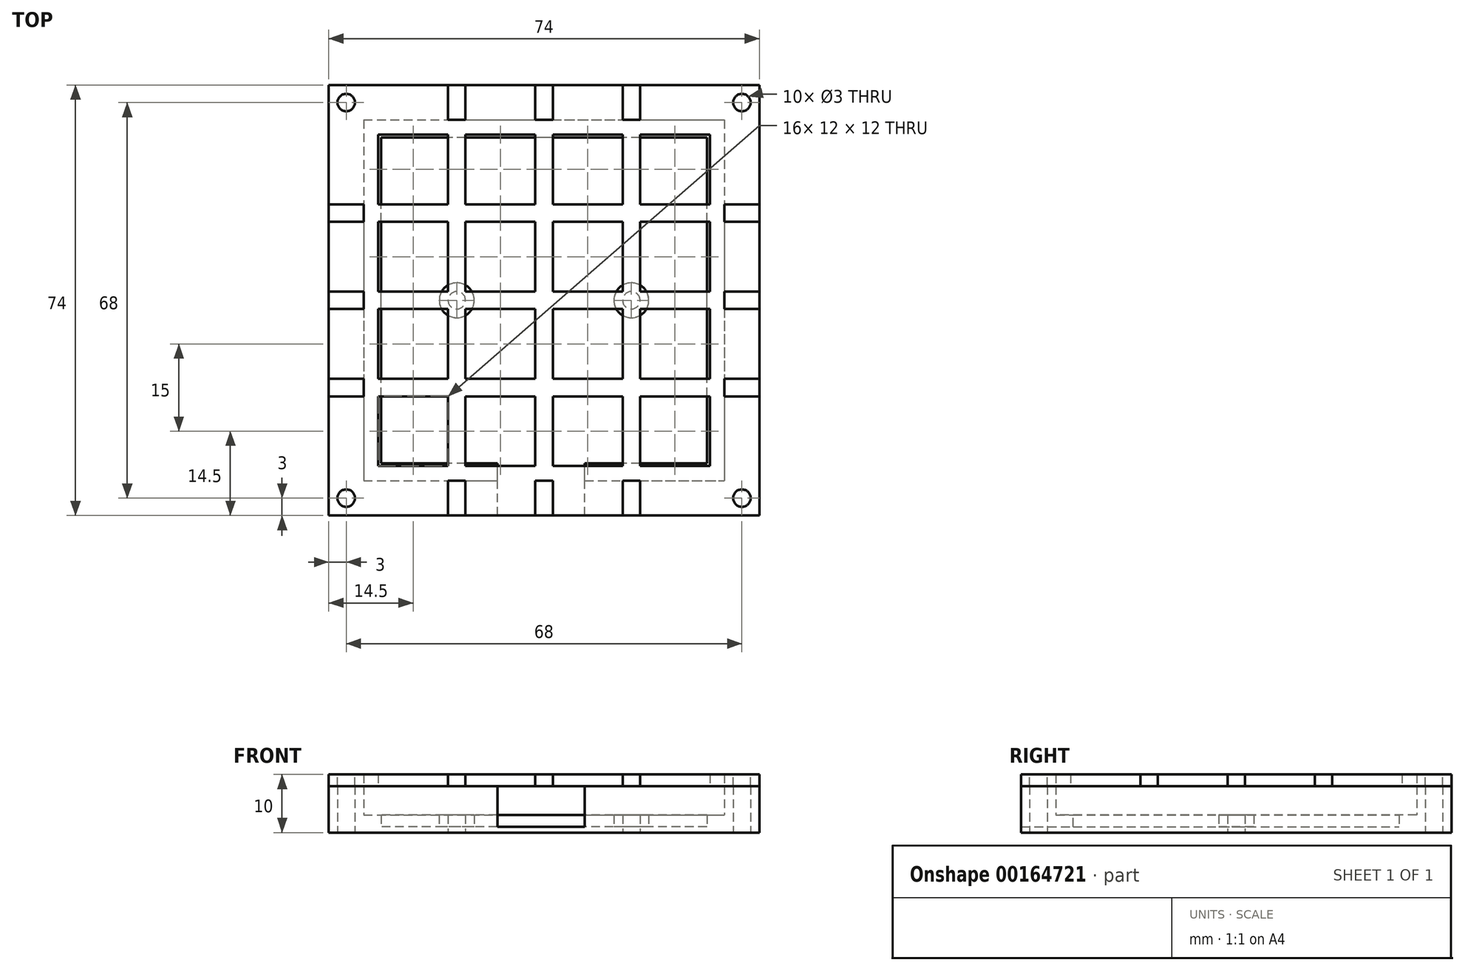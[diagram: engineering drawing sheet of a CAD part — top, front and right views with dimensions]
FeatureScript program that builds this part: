
annotation { "Feature Type Name" : "Feature", "Feature Type Description" : "" }
export const myFeature = defineFeature(function(context is Context, id is Id, definition is map)
    precondition{}
    {
        {
            var Q0;
            Q0=qCreatedBy(makeId("Top.planeOp"),FACE);
            var sketch = newSketch(context, id + "F0", { "sketchPlane" : qUnion([Q0])});
            skLineSegment(sketch, "E0.bottom", {"start": v(-31, 31) * mm, "end": v(31, 31) * mm});
            skLineSegment(sketch, "E0.top", {"start": v(-31, -31) * mm, "end": v(31, -31) * mm});
            skLineSegment(sketch, "E0.left", {"start": v(-31, 31) * mm, "end": v(-31, -31) * mm});
            skLineSegment(sketch, "E0.right", {"start": v(31, 31) * mm, "end": v(31, -31) * mm});
            skPoint(sketch, "E0.middle", {"position": v(0, 0) * mm});
            skLineSegment(sketch, "E1.bottom", {"start": v(-37, 37) * mm, "end": v(37, 37) * mm});
            skLineSegment(sketch, "E1.top", {"start": v(-37, -37) * mm, "end": v(37, -37) * mm});
            skLineSegment(sketch, "E1.left", {"start": v(-37, 37) * mm, "end": v(-37, -37) * mm});
            skLineSegment(sketch, "E1.right", {"start": v(37, 37) * mm, "end": v(37, -37) * mm});
            skCircle(sketch, "E2", {"center": v(34, 34) * mm, "radius": 1.5 * mm});
            skCircle(sketch, "E3", {"center": v(34, -34) * mm, "radius": 1.5 * mm});
            skCircle(sketch, "E4", {"center": v(-34, -34) * mm, "radius": 1.5 * mm});
            skCircle(sketch, "E5", {"center": v(-34, 34) * mm, "radius": 1.5 * mm});
            skCircle(sketch, "E6", {"center": v(-15, 0) * mm, "radius": 1.5 * mm});
            skCircle(sketch, "E7", {"center": v(15, 0) * mm, "radius": 1.5 * mm});
            skLineSegment(sketch, "E8", {"start": v(15, 0) * mm, "end": v(-15, 0) * mm, "construction": true});
            skCircle(sketch, "E9", {"center": v(-15, 0) * mm, "radius": 3 * mm});
            skCircle(sketch, "E10", {"center": v(15, 0) * mm, "radius": 3 * mm});
            skLineSegment(sketch, "E11.bottom", {"start": v(28, -28) * mm, "end": v(-28, -28) * mm});
            skLineSegment(sketch, "E11.top", {"start": v(28, 28) * mm, "end": v(-28, 28) * mm});
            skLineSegment(sketch, "E11.left", {"start": v(28, -28) * mm, "end": v(28, 28) * mm});
            skLineSegment(sketch, "E11.right", {"start": v(-28, -28) * mm, "end": v(-28, 28) * mm});
            skLineSegment(sketch, "E12", {"start": v(31, 31) * mm, "end": v(34, 31) * mm, "construction": true});
            skLineSegment(sketch, "E13", {"start": v(34, 31) * mm, "end": v(34, 34) * mm, "construction": true});
            skLineSegment(sketch, "E14", {"start": v(-31, 31) * mm, "end": v(-34, 31) * mm, "construction": true});
            skLineSegment(sketch, "E15", {"start": v(-34, 31) * mm, "end": v(-34, 34) * mm, "construction": true});
            skLineSegment(sketch, "E16", {"start": v(-31, -31) * mm, "end": v(-34, -31) * mm, "construction": true});
            skLineSegment(sketch, "E17", {"start": v(-34, -31) * mm, "end": v(-34, -34) * mm, "construction": true});
            skLineSegment(sketch, "E18", {"start": v(31, -31) * mm, "end": v(34, -31) * mm, "construction": true});
            skLineSegment(sketch, "E19", {"start": v(34, -31) * mm, "end": v(34, -34) * mm, "construction": true});
            skSolve(sketch);
        }
        {
            var Q0;
            Q0=makeQuery(id+"F0.imprint","IMPRINT",FACE,{"disambiguationData":[TD([[makeQuery(id+"F0.imprint","IMPRINT",EDGE,{"derivedFrom":sQuery(id+"F0.wireOp",EDGE,"E0.bottom")}),1.0]])]});
            extrude(context, id + "F1", {"entities" : qUnion([Q0]), "depth" : 8 * mm});
        }
        {
            var Q0;
            Q0=makeQuery(id+"F0.imprint","IMPRINT",FACE,{"disambiguationData":[TD([[makeQuery(id+"F0.imprint","IMPRINT",EDGE,{"derivedFrom":sQuery(id+"F0.wireOp",EDGE,"E0.bottom")}),-1.0]])]});
            extrude(context, id + "F2", {"entities" : qUnion([Q0]), "operationType" : NewBodyOperationType.ADD, "depth" : 2 * mm});
        }
        {
            var Q0;
            Q0=makeQuery(id+"F0.imprint","IMPRINT",FACE,{"disambiguationData":[TD([[makeQuery(id+"F0.imprint","IMPRINT",EDGE,{"derivedFrom":sQuery(id+"F0.wireOp",EDGE,"E9")}),-1.0]])]});
            extrude(context, id + "F3", {"entities" : qUnion([Q0]), "operationType" : NewBodyOperationType.ADD, "depth" : 1 * mm});
        }
        {
            var Q0;
            Q0=makeQuery(id+"F0.imprint","IMPRINT",FACE,{"disambiguationData":[TD([[makeQuery(id+"F0.imprint","IMPRINT",EDGE,{"derivedFrom":sQuery(id+"F0.wireOp",EDGE,"E6")}),-1.0]])]});
            var Q1;
            Q1=makeQuery(id+"F0.imprint","IMPRINT",FACE,{"disambiguationData":[TD([[makeQuery(id+"F0.imprint","IMPRINT",EDGE,{"derivedFrom":sQuery(id+"F0.wireOp",EDGE,"E7")}),-1.0]])]});
            extrude(context, id + "F4", {"entities" : qUnion([Q0, Q1]), "operationType" : NewBodyOperationType.ADD, "depth" : 3 * mm});
        }
        {
            var Q0;
            Q0=makeQuery(id+"F0.imprint","IMPRINT",FACE,{"disambiguationData":[TD([[makeQuery(id+"F0.imprint","IMPRINT",EDGE,{"derivedFrom":sQuery(id+"F0.wireOp",EDGE,"E0.bottom")}),-1.0]])]});
            extrude(context, id + "F5", {"entities" : qUnion([Q0]), "operationType" : NewBodyOperationType.ADD, "depth" : 3 * mm});
        }
        {
            var Q0;
            Q0=makeQuery(id+"F1.opExtrude","CAP_FACE",FACE,{"disambiguationData":[OSD([sQuery(id+"F0.wireOp",EDGE,"E0.bottom"),sQuery(id+"F0.wireOp",EDGE,"E0.top"),sQuery(id+"F0.wireOp",EDGE,"E0.left"),sQuery(id+"F0.wireOp",EDGE,"E0.right"),sQuery(id+"F0.wireOp",EDGE,"E1.bottom"),sQuery(id+"F0.wireOp",EDGE,"E1.top"),sQuery(id+"F0.wireOp",EDGE,"E1.left"),sQuery(id+"F0.wireOp",EDGE,"E1.right"),sQuery(id+"F0.wireOp",EDGE,"E2"),sQuery(id+"F0.wireOp",EDGE,"E3"),sQuery(id+"F0.wireOp",EDGE,"E4"),sQuery(id+"F0.wireOp",EDGE,"E5")])],"isStart":false});
            var sketch = newSketch(context, id + "F6", { "sketchPlane" : qUnion([Q0])});
            skLineSegment(sketch, "E20", {"start": v(-0.5, -37) * mm, "end": v(-0.5, -31) * mm, "construction": true});
            skLineSegment(sketch, "E21.0", {"start": v(28, -28) * mm, "end": v(-28, -28) * mm});
            skLineSegment(sketch, "E22.bottom", {"start": v(-0.5, -37) * mm, "end": v(-8, -37) * mm});
            skLineSegment(sketch, "E22.top", {"start": v(-0.5, -28) * mm, "end": v(-8, -28) * mm});
            skLineSegment(sketch, "E22.left", {"start": v(-0.5, -37) * mm, "end": v(-0.5, -28) * mm});
            skLineSegment(sketch, "E22.right", {"start": v(-8, -37) * mm, "end": v(-8, -28) * mm});
            skLineSegment(sketch, "E23.bottom", {"start": v(-0.5, -37) * mm, "end": v(7, -37) * mm});
            skLineSegment(sketch, "E23.top", {"start": v(-0.5, -28) * mm, "end": v(7, -28) * mm});
            skLineSegment(sketch, "E23.right", {"start": v(7, -37) * mm, "end": v(7, -28) * mm});
            skSolve(sketch);
        }
        {
            var Q0;
            Q0=makeQuery(id+"F1.opExtrude","CAP_FACE",FACE,{"disambiguationData":[OSD([sQuery(id+"F0.wireOp",EDGE,"E0.bottom"),sQuery(id+"F0.wireOp",EDGE,"E0.top"),sQuery(id+"F0.wireOp",EDGE,"E0.left"),sQuery(id+"F0.wireOp",EDGE,"E0.right"),sQuery(id+"F0.wireOp",EDGE,"E1.bottom"),sQuery(id+"F0.wireOp",EDGE,"E1.top"),sQuery(id+"F0.wireOp",EDGE,"E1.left"),sQuery(id+"F0.wireOp",EDGE,"E1.right"),sQuery(id+"F0.wireOp",EDGE,"E2"),sQuery(id+"F0.wireOp",EDGE,"E3"),sQuery(id+"F0.wireOp",EDGE,"E4"),sQuery(id+"F0.wireOp",EDGE,"E5")])],"isStart":false});
            var sketch = newSketch(context, id + "F7", { "sketchPlane" : qUnion([Q0])});
            skLineSegment(sketch, "E24.bottom", {"start": v(-37, 37) * mm, "end": v(37, 37) * mm});
            skLineSegment(sketch, "E24.top", {"start": v(-37, -37) * mm, "end": v(37, -37) * mm});
            skLineSegment(sketch, "E24.left", {"start": v(-37, 37) * mm, "end": v(-37, -37) * mm});
            skLineSegment(sketch, "E24.right", {"start": v(37, 37) * mm, "end": v(37, -37) * mm});
            skLineSegment(sketch, "E25", {"start": v(-15, 37) * mm, "end": v(-15, -36.5) * mm, "construction": true});
            skLineSegment(sketch, "E26", {"start": v(0, 37) * mm, "end": v(0, -37) * mm, "construction": true});
            skLineSegment(sketch, "E27", {"start": v(15, 37) * mm, "end": v(15, -37) * mm, "construction": true});
            skLineSegment(sketch, "E28", {"start": v(-31, 0) * mm, "end": v(31, 0) * mm, "construction": true});
            skLineSegment(sketch, "E29", {"start": v(-31, 15) * mm, "end": v(31, 15) * mm, "construction": true});
            skLineSegment(sketch, "E30", {"start": v(-31, -15) * mm, "end": v(31, -15) * mm, "construction": true});
            skLineSegment(sketch, "E31.bottom", {"start": v(-16.5, 37) * mm, "end": v(-13.5, 37) * mm});
            skLineSegment(sketch, "E31.top", {"start": v(-16.5, -37) * mm, "end": v(-13.5, -37) * mm});
            skLineSegment(sketch, "E31.left", {"start": v(-16.5, 37) * mm, "end": v(-16.5, -37) * mm});
            skLineSegment(sketch, "E31.right", {"start": v(-13.5, 37) * mm, "end": v(-13.5, -37) * mm});
            skLineSegment(sketch, "E32.bottom", {"start": v(-1.5, 37) * mm, "end": v(1.5, 37) * mm});
            skLineSegment(sketch, "E32.top", {"start": v(-1.5, -37) * mm, "end": v(1.5, -37) * mm});
            skLineSegment(sketch, "E32.left", {"start": v(-1.5, 37) * mm, "end": v(-1.5, -37) * mm});
            skLineSegment(sketch, "E32.right", {"start": v(1.5, 37) * mm, "end": v(1.5, -37) * mm});
            skLineSegment(sketch, "E33.bottom", {"start": v(13.5, 37) * mm, "end": v(16.5, 37) * mm});
            skLineSegment(sketch, "E33.top", {"start": v(13.5, -37) * mm, "end": v(16.5, -37) * mm});
            skLineSegment(sketch, "E33.left", {"start": v(13.5, 37) * mm, "end": v(13.5, -37) * mm});
            skLineSegment(sketch, "E33.right", {"start": v(16.5, 37) * mm, "end": v(16.5, -37) * mm});
            skLineSegment(sketch, "E34.bottom", {"start": v(-37, 13.5) * mm, "end": v(37, 13.5) * mm});
            skLineSegment(sketch, "E34.top", {"start": v(-37, 16.5) * mm, "end": v(37, 16.5) * mm});
            skLineSegment(sketch, "E34.left", {"start": v(-37, 13.5) * mm, "end": v(-37, 16.5) * mm});
            skLineSegment(sketch, "E34.right", {"start": v(37, 13.5) * mm, "end": v(37, 16.5) * mm});
            skLineSegment(sketch, "E35.bottom", {"start": v(-37, -1.5) * mm, "end": v(37, -1.5) * mm});
            skLineSegment(sketch, "E35.top", {"start": v(-37, 1.5) * mm, "end": v(37, 1.5) * mm});
            skLineSegment(sketch, "E35.left", {"start": v(-37, -1.5) * mm, "end": v(-37, 1.5) * mm});
            skLineSegment(sketch, "E35.right", {"start": v(37, -1.5) * mm, "end": v(37, 1.5) * mm});
            skLineSegment(sketch, "E36.bottom", {"start": v(-37, -16.5) * mm, "end": v(37, -16.5) * mm});
            skLineSegment(sketch, "E36.top", {"start": v(-37, -13.5) * mm, "end": v(37, -13.5) * mm});
            skLineSegment(sketch, "E36.left", {"start": v(-37, -16.5) * mm, "end": v(-37, -13.5) * mm});
            skLineSegment(sketch, "E36.right", {"start": v(37, -16.5) * mm, "end": v(37, -13.5) * mm});
            skLineSegment(sketch, "E37", {"start": v(-31, -15) * mm, "end": v(-37, -15) * mm, "construction": true});
            skLineSegment(sketch, "E38", {"start": v(-31, 0) * mm, "end": v(-37, 0) * mm, "construction": true});
            skLineSegment(sketch, "E39", {"start": v(-31, 15) * mm, "end": v(-37, 15) * mm, "construction": true});
            skLineSegment(sketch, "E40.bottom", {"start": v(28.5, -28.5) * mm, "end": v(-28.5, -28.5) * mm});
            skLineSegment(sketch, "E40.top", {"start": v(28.5, 28.5) * mm, "end": v(-28.5, 28.5) * mm});
            skLineSegment(sketch, "E40.left", {"start": v(28.5, -28.5) * mm, "end": v(28.5, 28.5) * mm});
            skLineSegment(sketch, "E40.right", {"start": v(-28.5, -28.5) * mm, "end": v(-28.5, 28.5) * mm});
            skPoint(sketch, "E40.middle", {"position": v(0, 0) * mm});
            skSolve(sketch);
        }
        {
            var Q0;
            Q0=makeQuery(id+"F7.imprint","IMPRINT",FACE,{"disambiguationData":[TD([[makeQuery(id+"F7.imprint","IMPRINT",EDGE,{"derivedFrom":makeQuery(id+"F1.opExtrude","CAP_EDGE",EDGE,{"disambiguationData":[OSD([sQuery(id+"F0.wireOp",EDGE,"E5")])],"isStart":false})}),-1.0]])]});
            var Q1;
            {var subQ0=sQuery(id+"F7.wireOp",EDGE,"E31.right");var subQ5=makeQuery(id+"F1.opExtrude","CAP_EDGE",EDGE,{"disambiguationData":[OSD([sQuery(id+"F0.wireOp",EDGE,"E0.bottom")])],"isStart":false});var subQ6=makeQuery(id+"F7.imprint","INTERSECT",VERTEX,{"derivedFrom":[subQ5,subQ0]});Q1=makeQuery(id+"F7.imprint","IMPRINT",FACE,{"disambiguationData":[TD([[makeQuery(id+"F7.imprint","IMPRINT",EDGE,{"disambiguationData":[TD([[subQ6,-1.0]])],"derivedFrom":subQ5}),1.0]])]});}
            var Q2;
            {var subQ0=sQuery(id+"F7.wireOp",EDGE,"E31.bottom");Q2=makeQuery(id+"F7.imprint","IMPRINT",FACE,{"disambiguationData":[TD([[makeQuery(id+"F7.imprint","IMPRINT",EDGE,{"derivedFrom":subQ0}),-1.0]])]});}
            var Q3;
            {var subQ0=sQuery(id+"F7.wireOp",EDGE,"E32.bottom");Q3=makeQuery(id+"F7.imprint","IMPRINT",FACE,{"disambiguationData":[TD([[makeQuery(id+"F7.imprint","IMPRINT",EDGE,{"derivedFrom":subQ0}),-1.0]])]});}
            var Q4;
            {var subQ0=sQuery(id+"F7.wireOp",EDGE,"E32.right");var subQ5=makeQuery(id+"F1.opExtrude","CAP_EDGE",EDGE,{"disambiguationData":[OSD([sQuery(id+"F0.wireOp",EDGE,"E0.bottom")])],"isStart":false});var subQ6=makeQuery(id+"F7.imprint","INTERSECT",VERTEX,{"derivedFrom":[subQ5,subQ0]});Q4=makeQuery(id+"F7.imprint","IMPRINT",FACE,{"disambiguationData":[TD([[makeQuery(id+"F7.imprint","IMPRINT",EDGE,{"disambiguationData":[TD([[subQ6,-1.0]])],"derivedFrom":subQ5}),1.0]])]});}
            var Q5;
            {var subQ0=sQuery(id+"F7.wireOp",EDGE,"E33.bottom");Q5=makeQuery(id+"F7.imprint","IMPRINT",FACE,{"disambiguationData":[TD([[makeQuery(id+"F7.imprint","IMPRINT",EDGE,{"derivedFrom":subQ0}),-1.0]])]});}
            var Q6;
            Q6=makeQuery(id+"F7.imprint","IMPRINT",FACE,{"disambiguationData":[TD([[makeQuery(id+"F7.imprint","IMPRINT",EDGE,{"derivedFrom":makeQuery(id+"F1.opExtrude","CAP_EDGE",EDGE,{"disambiguationData":[OSD([sQuery(id+"F0.wireOp",EDGE,"E2")])],"isStart":false})}),-1.0]])]});
            var Q7;
            {var subQ1=sQuery(id+"F7.wireOp",EDGE,"E40.top");var subQ5=sQuery(id+"F7.wireOp",EDGE,"E33.right");var subQ6=makeQuery(id+"F7.imprint","INTERSECT",VERTEX,{"derivedFrom":[subQ5,subQ1]});Q7=makeQuery(id+"F7.imprint","IMPRINT",FACE,{"disambiguationData":[TD([[makeQuery(id+"F7.imprint","IMPRINT",EDGE,{"disambiguationData":[TD([[subQ6,1.0]])],"derivedFrom":subQ5}),1.0]])]});}
            var Q8;
            {var subQ0=sQuery(id+"F7.wireOp",EDGE,"E40.top");var subQ1=sQuery(id+"F7.wireOp",EDGE,"E33.left");var subQ2=makeQuery(id+"F7.imprint","INTERSECT",VERTEX,{"derivedFrom":[subQ1,subQ0]});Q8=makeQuery(id+"F7.imprint","IMPRINT",FACE,{"disambiguationData":[TD([[makeQuery(id+"F7.imprint","IMPRINT",EDGE,{"disambiguationData":[TD([[subQ2,1.0]])],"derivedFrom":subQ1}),1.0]])]});}
            var Q9;
            {var subQ0=sQuery(id+"F7.wireOp",EDGE,"E40.top");var subQ1=sQuery(id+"F7.wireOp",EDGE,"E32.right");var subQ2=makeQuery(id+"F7.imprint","INTERSECT",VERTEX,{"derivedFrom":[subQ1,subQ0]});Q9=makeQuery(id+"F7.imprint","IMPRINT",FACE,{"disambiguationData":[TD([[makeQuery(id+"F7.imprint","IMPRINT",EDGE,{"disambiguationData":[TD([[subQ2,1.0]])],"derivedFrom":subQ1}),1.0]])]});}
            var Q10;
            {var subQ0=sQuery(id+"F7.wireOp",EDGE,"E40.top");var subQ1=sQuery(id+"F7.wireOp",EDGE,"E32.left");var subQ2=makeQuery(id+"F7.imprint","INTERSECT",VERTEX,{"derivedFrom":[subQ1,subQ0]});Q10=makeQuery(id+"F7.imprint","IMPRINT",FACE,{"disambiguationData":[TD([[makeQuery(id+"F7.imprint","IMPRINT",EDGE,{"disambiguationData":[TD([[subQ2,1.0]])],"derivedFrom":subQ1}),1.0]])]});}
            var Q11;
            {var subQ0=sQuery(id+"F7.wireOp",EDGE,"E40.top");var subQ1=sQuery(id+"F7.wireOp",EDGE,"E31.right");var subQ2=makeQuery(id+"F7.imprint","INTERSECT",VERTEX,{"derivedFrom":[subQ1,subQ0]});Q11=makeQuery(id+"F7.imprint","IMPRINT",FACE,{"disambiguationData":[TD([[makeQuery(id+"F7.imprint","IMPRINT",EDGE,{"disambiguationData":[TD([[subQ2,1.0]])],"derivedFrom":subQ1}),1.0]])]});}
            var Q12;
            {var subQ0=sQuery(id+"F7.wireOp",EDGE,"E40.top");var subQ1=sQuery(id+"F7.wireOp",EDGE,"E31.left");var subQ2=makeQuery(id+"F7.imprint","INTERSECT",VERTEX,{"derivedFrom":[subQ1,subQ0]});Q12=makeQuery(id+"F7.imprint","IMPRINT",FACE,{"disambiguationData":[TD([[makeQuery(id+"F7.imprint","IMPRINT",EDGE,{"disambiguationData":[TD([[subQ2,1.0]])],"derivedFrom":subQ1}),1.0]])]});}
            var Q13;
            {var subQ5=sQuery(id+"F7.wireOp",EDGE,"E40.top");var subQ7=sQuery(id+"F7.wireOp",EDGE,"E31.left");var subQ8=makeQuery(id+"F7.imprint","INTERSECT",VERTEX,{"derivedFrom":[subQ7,subQ5]});Q13=makeQuery(id+"F7.imprint","IMPRINT",FACE,{"disambiguationData":[TD([[makeQuery(id+"F7.imprint","IMPRINT",EDGE,{"disambiguationData":[TD([[subQ8,1.0]])],"derivedFrom":subQ7}),-1.0]])]});}
            var Q14;
            {var subQ0=sQuery(id+"F7.wireOp",EDGE,"E34.left");Q14=makeQuery(id+"F7.imprint","IMPRINT",FACE,{"disambiguationData":[TD([[makeQuery(id+"F7.imprint","IMPRINT",EDGE,{"derivedFrom":subQ0}),1.0]])]});}
            var Q15;
            {var subQ0=sQuery(id+"F7.wireOp",EDGE,"E40.right");var subQ1=sQuery(id+"F7.wireOp",EDGE,"E34.bottom");var subQ2=makeQuery(id+"F7.imprint","INTERSECT",VERTEX,{"derivedFrom":[subQ1,subQ0]});Q15=makeQuery(id+"F7.imprint","IMPRINT",FACE,{"disambiguationData":[TD([[makeQuery(id+"F7.imprint","IMPRINT",EDGE,{"disambiguationData":[TD([[subQ2,1.0]])],"derivedFrom":subQ1}),1.0]])]});}
            var Q16;
            {var subQ0=sQuery(id+"F7.wireOp",EDGE,"E35.left");Q16=makeQuery(id+"F7.imprint","IMPRINT",FACE,{"disambiguationData":[TD([[makeQuery(id+"F7.imprint","IMPRINT",EDGE,{"derivedFrom":subQ0}),1.0]])]});}
            var Q17;
            {var subQ0=sQuery(id+"F7.wireOp",EDGE,"E40.right");var subQ1=sQuery(id+"F7.wireOp",EDGE,"E35.bottom");var subQ2=makeQuery(id+"F7.imprint","INTERSECT",VERTEX,{"derivedFrom":[subQ1,subQ0]});Q17=makeQuery(id+"F7.imprint","IMPRINT",FACE,{"disambiguationData":[TD([[makeQuery(id+"F7.imprint","IMPRINT",EDGE,{"disambiguationData":[TD([[subQ2,1.0]])],"derivedFrom":subQ1}),1.0]])]});}
            var Q18;
            {var subQ0=sQuery(id+"F7.wireOp",EDGE,"E34.bottom");var subQ5=makeQuery(id+"F1.opExtrude","CAP_EDGE",EDGE,{"disambiguationData":[OSD([sQuery(id+"F0.wireOp",EDGE,"E0.left")])],"isStart":false});var subQ7=makeQuery(id+"F7.imprint","INTERSECT",VERTEX,{"derivedFrom":[subQ5,subQ0]});Q18=makeQuery(id+"F7.imprint","IMPRINT",FACE,{"disambiguationData":[TD([[makeQuery(id+"F7.imprint","IMPRINT",EDGE,{"disambiguationData":[TD([[subQ7,-1.0]])],"derivedFrom":subQ5}),-1.0]])]});}
            var Q19;
            {var subQ0=sQuery(id+"F7.wireOp",EDGE,"E40.right");var subQ1=sQuery(id+"F7.wireOp",EDGE,"E34.bottom");var subQ2=makeQuery(id+"F7.imprint","INTERSECT",VERTEX,{"derivedFrom":[subQ1,subQ0]});Q19=makeQuery(id+"F7.imprint","IMPRINT",FACE,{"disambiguationData":[TD([[makeQuery(id+"F7.imprint","IMPRINT",EDGE,{"disambiguationData":[TD([[subQ2,1.0]])],"derivedFrom":subQ1}),-1.0]])]});}
            var Q20;
            {var subQ0=sQuery(id+"F7.wireOp",EDGE,"E35.bottom");var subQ5=makeQuery(id+"F1.opExtrude","CAP_EDGE",EDGE,{"disambiguationData":[OSD([sQuery(id+"F0.wireOp",EDGE,"E0.left")])],"isStart":false});var subQ6=makeQuery(id+"F7.imprint","INTERSECT",VERTEX,{"derivedFrom":[subQ5,subQ0]});Q20=makeQuery(id+"F7.imprint","IMPRINT",FACE,{"disambiguationData":[TD([[makeQuery(id+"F7.imprint","IMPRINT",EDGE,{"disambiguationData":[TD([[subQ6,-1.0]])],"derivedFrom":subQ5}),-1.0]])]});}
            var Q21;
            {var subQ0=sQuery(id+"F7.wireOp",EDGE,"E40.right");var subQ1=sQuery(id+"F7.wireOp",EDGE,"E35.bottom");var subQ2=makeQuery(id+"F7.imprint","INTERSECT",VERTEX,{"derivedFrom":[subQ1,subQ0]});Q21=makeQuery(id+"F7.imprint","IMPRINT",FACE,{"disambiguationData":[TD([[makeQuery(id+"F7.imprint","IMPRINT",EDGE,{"disambiguationData":[TD([[subQ2,1.0]])],"derivedFrom":subQ1}),-1.0]])]});}
            var Q22;
            {var subQ0=sQuery(id+"F7.wireOp",EDGE,"E36.left");Q22=makeQuery(id+"F7.imprint","IMPRINT",FACE,{"disambiguationData":[TD([[makeQuery(id+"F7.imprint","IMPRINT",EDGE,{"derivedFrom":subQ0}),1.0]])]});}
            var Q23;
            {var subQ0=sQuery(id+"F7.wireOp",EDGE,"E40.right");var subQ1=sQuery(id+"F7.wireOp",EDGE,"E36.bottom");var subQ2=makeQuery(id+"F7.imprint","INTERSECT",VERTEX,{"derivedFrom":[subQ1,subQ0]});Q23=makeQuery(id+"F7.imprint","IMPRINT",FACE,{"disambiguationData":[TD([[makeQuery(id+"F7.imprint","IMPRINT",EDGE,{"disambiguationData":[TD([[subQ2,1.0]])],"derivedFrom":subQ1}),1.0]])]});}
            var Q24;
            {var subQ3=sQuery(id+"F0.wireOp",EDGE,"E4");Q24=makeQuery(id+"F7.imprint","IMPRINT",FACE,{"disambiguationData":[TD([[makeQuery(id+"F7.imprint","IMPRINT",EDGE,{"derivedFrom":makeQuery(id+"F1.opExtrude","CAP_EDGE",EDGE,{"disambiguationData":[OSD([subQ3])],"isStart":false})}),-1.0]])]});}
            var Q25;
            {var subQ0=sQuery(id+"F7.wireOp",EDGE,"E40.right");var subQ3=sQuery(id+"F7.wireOp",EDGE,"E36.bottom");var subQ4=makeQuery(id+"F7.imprint","INTERSECT",VERTEX,{"derivedFrom":[subQ3,subQ0]});Q25=makeQuery(id+"F7.imprint","IMPRINT",FACE,{"disambiguationData":[TD([[makeQuery(id+"F7.imprint","IMPRINT",EDGE,{"disambiguationData":[TD([[subQ4,1.0]])],"derivedFrom":subQ3}),-1.0]])]});}
            var Q26;
            {var subQ0=sQuery(id+"F7.wireOp",EDGE,"E31.top");Q26=makeQuery(id+"F7.imprint","IMPRINT",FACE,{"disambiguationData":[TD([[makeQuery(id+"F7.imprint","IMPRINT",EDGE,{"derivedFrom":subQ0}),1.0]])]});}
            var Q27;
            {var subQ0=sQuery(id+"F7.wireOp",EDGE,"E40.bottom");var subQ1=sQuery(id+"F7.wireOp",EDGE,"E31.left");var subQ2=makeQuery(id+"F7.imprint","INTERSECT",VERTEX,{"derivedFrom":[subQ1,subQ0]});Q27=makeQuery(id+"F7.imprint","IMPRINT",FACE,{"disambiguationData":[TD([[makeQuery(id+"F7.imprint","IMPRINT",EDGE,{"disambiguationData":[TD([[subQ2,1.0]])],"derivedFrom":subQ0}),1.0]])]});}
            var Q28;
            {var subQ0=sQuery(id+"F7.wireOp",EDGE,"E32.top");Q28=makeQuery(id+"F7.imprint","IMPRINT",FACE,{"disambiguationData":[TD([[makeQuery(id+"F7.imprint","IMPRINT",EDGE,{"derivedFrom":subQ0}),1.0]])]});}
            var Q29;
            {var subQ0=sQuery(id+"F7.wireOp",EDGE,"E33.top");Q29=makeQuery(id+"F7.imprint","IMPRINT",FACE,{"disambiguationData":[TD([[makeQuery(id+"F7.imprint","IMPRINT",EDGE,{"derivedFrom":subQ0}),1.0]])]});}
            var Q30;
            {var subQ0=sQuery(id+"F7.wireOp",EDGE,"E40.bottom");var subQ1=sQuery(id+"F7.wireOp",EDGE,"E33.left");var subQ2=makeQuery(id+"F7.imprint","INTERSECT",VERTEX,{"derivedFrom":[subQ1,subQ0]});Q30=makeQuery(id+"F7.imprint","IMPRINT",FACE,{"disambiguationData":[TD([[makeQuery(id+"F7.imprint","IMPRINT",EDGE,{"disambiguationData":[TD([[subQ2,1.0]])],"derivedFrom":subQ0}),1.0]])]});}
            var Q31;
            {var subQ10=sQuery(id+"F0.wireOp",EDGE,"E3");Q31=makeQuery(id+"F7.imprint","IMPRINT",FACE,{"disambiguationData":[TD([[makeQuery(id+"F7.imprint","IMPRINT",EDGE,{"derivedFrom":makeQuery(id+"F1.opExtrude","CAP_EDGE",EDGE,{"disambiguationData":[OSD([subQ10])],"isStart":false})}),-1.0]])]});}
            var Q32;
            Q32=makeQuery(id+"F7.imprint","IMPRINT",FACE,{"disambiguationData":[TD([[makeQuery(id+"F7.imprint","IMPRINT",EDGE,{"derivedFrom":makeQuery(id+"F1.opExtrude","CAP_EDGE",EDGE,{"disambiguationData":[OSD([sQuery(id+"F0.wireOp",EDGE,"E3")])],"isStart":false})}),1.0]])]});
            var Q33;
            {var subQ0=sQuery(id+"F7.wireOp",EDGE,"E40.left");var subQ3=sQuery(id+"F7.wireOp",EDGE,"E36.bottom");var subQ4=makeQuery(id+"F7.imprint","INTERSECT",VERTEX,{"derivedFrom":[subQ3,subQ0]});Q33=makeQuery(id+"F7.imprint","IMPRINT",FACE,{"disambiguationData":[TD([[makeQuery(id+"F7.imprint","IMPRINT",EDGE,{"disambiguationData":[TD([[subQ4,-1.0]])],"derivedFrom":subQ3}),-1.0]])]});}
            var Q34;
            {var subQ0=sQuery(id+"F7.wireOp",EDGE,"E36.right");Q34=makeQuery(id+"F7.imprint","IMPRINT",FACE,{"disambiguationData":[TD([[makeQuery(id+"F7.imprint","IMPRINT",EDGE,{"derivedFrom":subQ0}),-1.0]])]});}
            var Q35;
            {var subQ0=sQuery(id+"F7.wireOp",EDGE,"E40.left");var subQ1=sQuery(id+"F7.wireOp",EDGE,"E36.bottom");var subQ2=makeQuery(id+"F7.imprint","INTERSECT",VERTEX,{"derivedFrom":[subQ1,subQ0]});Q35=makeQuery(id+"F7.imprint","IMPRINT",FACE,{"disambiguationData":[TD([[makeQuery(id+"F7.imprint","IMPRINT",EDGE,{"disambiguationData":[TD([[subQ2,-1.0]])],"derivedFrom":subQ1}),1.0]])]});}
            var Q36;
            {var subQ0=sQuery(id+"F7.wireOp",EDGE,"E35.bottom");var subQ5=makeQuery(id+"F1.opExtrude","CAP_EDGE",EDGE,{"disambiguationData":[OSD([sQuery(id+"F0.wireOp",EDGE,"E0.right")])],"isStart":false});var subQ6=makeQuery(id+"F7.imprint","INTERSECT",VERTEX,{"derivedFrom":[subQ5,subQ0]});Q36=makeQuery(id+"F7.imprint","IMPRINT",FACE,{"disambiguationData":[TD([[makeQuery(id+"F7.imprint","IMPRINT",EDGE,{"disambiguationData":[TD([[subQ6,-1.0]])],"derivedFrom":subQ5}),1.0]])]});}
            var Q37;
            {var subQ0=sQuery(id+"F7.wireOp",EDGE,"E40.left");var subQ1=sQuery(id+"F7.wireOp",EDGE,"E35.bottom");var subQ2=makeQuery(id+"F7.imprint","INTERSECT",VERTEX,{"derivedFrom":[subQ1,subQ0]});Q37=makeQuery(id+"F7.imprint","IMPRINT",FACE,{"disambiguationData":[TD([[makeQuery(id+"F7.imprint","IMPRINT",EDGE,{"disambiguationData":[TD([[subQ2,-1.0]])],"derivedFrom":subQ1}),-1.0]])]});}
            var Q38;
            {var subQ0=sQuery(id+"F7.wireOp",EDGE,"E40.left");var subQ1=sQuery(id+"F7.wireOp",EDGE,"E35.bottom");var subQ2=makeQuery(id+"F7.imprint","INTERSECT",VERTEX,{"derivedFrom":[subQ1,subQ0]});Q38=makeQuery(id+"F7.imprint","IMPRINT",FACE,{"disambiguationData":[TD([[makeQuery(id+"F7.imprint","IMPRINT",EDGE,{"disambiguationData":[TD([[subQ2,-1.0]])],"derivedFrom":subQ1}),1.0]])]});}
            var Q39;
            {var subQ0=sQuery(id+"F7.wireOp",EDGE,"E35.right");Q39=makeQuery(id+"F7.imprint","IMPRINT",FACE,{"disambiguationData":[TD([[makeQuery(id+"F7.imprint","IMPRINT",EDGE,{"derivedFrom":subQ0}),-1.0]])]});}
            var Q40;
            {var subQ0=sQuery(id+"F7.wireOp",EDGE,"E34.bottom");var subQ5=makeQuery(id+"F1.opExtrude","CAP_EDGE",EDGE,{"disambiguationData":[OSD([sQuery(id+"F0.wireOp",EDGE,"E0.right")])],"isStart":false});var subQ7=makeQuery(id+"F7.imprint","INTERSECT",VERTEX,{"derivedFrom":[subQ5,subQ0]});Q40=makeQuery(id+"F7.imprint","IMPRINT",FACE,{"disambiguationData":[TD([[makeQuery(id+"F7.imprint","IMPRINT",EDGE,{"disambiguationData":[TD([[subQ7,-1.0]])],"derivedFrom":subQ5}),1.0]])]});}
            var Q41;
            {var subQ0=sQuery(id+"F7.wireOp",EDGE,"E40.left");var subQ1=sQuery(id+"F7.wireOp",EDGE,"E34.bottom");var subQ2=makeQuery(id+"F7.imprint","INTERSECT",VERTEX,{"derivedFrom":[subQ1,subQ0]});Q41=makeQuery(id+"F7.imprint","IMPRINT",FACE,{"disambiguationData":[TD([[makeQuery(id+"F7.imprint","IMPRINT",EDGE,{"disambiguationData":[TD([[subQ2,-1.0]])],"derivedFrom":subQ1}),-1.0]])]});}
            var Q42;
            {var subQ0=sQuery(id+"F7.wireOp",EDGE,"E34.right");Q42=makeQuery(id+"F7.imprint","IMPRINT",FACE,{"disambiguationData":[TD([[makeQuery(id+"F7.imprint","IMPRINT",EDGE,{"derivedFrom":subQ0}),-1.0]])]});}
            var Q43;
            {var subQ0=sQuery(id+"F7.wireOp",EDGE,"E40.left");var subQ1=sQuery(id+"F7.wireOp",EDGE,"E34.bottom");var subQ2=makeQuery(id+"F7.imprint","INTERSECT",VERTEX,{"derivedFrom":[subQ1,subQ0]});Q43=makeQuery(id+"F7.imprint","IMPRINT",FACE,{"disambiguationData":[TD([[makeQuery(id+"F7.imprint","IMPRINT",EDGE,{"disambiguationData":[TD([[subQ2,-1.0]])],"derivedFrom":subQ1}),1.0]])]});}
            var Q44;
            {var subQ0=sQuery(id+"F7.wireOp",EDGE,"E34.top");var subQ1=sQuery(id+"F7.wireOp",EDGE,"E33.right");var subQ2=makeQuery(id+"F7.imprint","INTERSECT",VERTEX,{"derivedFrom":[subQ1,subQ0]});Q44=makeQuery(id+"F7.imprint","IMPRINT",FACE,{"disambiguationData":[TD([[makeQuery(id+"F7.imprint","IMPRINT",EDGE,{"disambiguationData":[TD([[subQ2,-1.0]])],"derivedFrom":subQ1}),1.0]])]});}
            var Q45;
            {var subQ0=sQuery(id+"F7.wireOp",EDGE,"E40.top");var subQ1=sQuery(id+"F7.wireOp",EDGE,"E33.left");var subQ2=makeQuery(id+"F7.imprint","INTERSECT",VERTEX,{"derivedFrom":[subQ1,subQ0]});Q45=makeQuery(id+"F7.imprint","IMPRINT",FACE,{"disambiguationData":[TD([[makeQuery(id+"F7.imprint","IMPRINT",EDGE,{"disambiguationData":[TD([[subQ2,-1.0]])],"derivedFrom":subQ1}),1.0]])]});}
            var Q46;
            {var subQ0=sQuery(id+"F7.wireOp",EDGE,"E34.top");var subQ1=sQuery(id+"F7.wireOp",EDGE,"E33.left");var subQ2=makeQuery(id+"F7.imprint","INTERSECT",VERTEX,{"derivedFrom":[subQ1,subQ0]});Q46=makeQuery(id+"F7.imprint","IMPRINT",FACE,{"disambiguationData":[TD([[makeQuery(id+"F7.imprint","IMPRINT",EDGE,{"disambiguationData":[TD([[subQ2,-1.0]])],"derivedFrom":subQ1}),1.0]])]});}
            var Q47;
            {var subQ0=sQuery(id+"F7.wireOp",EDGE,"E34.top");var subQ1=sQuery(id+"F7.wireOp",EDGE,"E31.left");var subQ2=makeQuery(id+"F7.imprint","INTERSECT",VERTEX,{"derivedFrom":[subQ1,subQ0]});Q47=makeQuery(id+"F7.imprint","IMPRINT",FACE,{"disambiguationData":[TD([[makeQuery(id+"F7.imprint","IMPRINT",EDGE,{"disambiguationData":[TD([[subQ2,-1.0]])],"derivedFrom":subQ1}),-1.0]])]});}
            var Q48;
            {var subQ0=sQuery(id+"F7.wireOp",EDGE,"E40.top");var subQ1=sQuery(id+"F7.wireOp",EDGE,"E31.left");var subQ2=makeQuery(id+"F7.imprint","INTERSECT",VERTEX,{"derivedFrom":[subQ1,subQ0]});Q48=makeQuery(id+"F7.imprint","IMPRINT",FACE,{"disambiguationData":[TD([[makeQuery(id+"F7.imprint","IMPRINT",EDGE,{"disambiguationData":[TD([[subQ2,-1.0]])],"derivedFrom":subQ1}),1.0]])]});}
            var Q49;
            {var subQ0=sQuery(id+"F7.wireOp",EDGE,"E34.top");var subQ1=sQuery(id+"F7.wireOp",EDGE,"E31.left");var subQ2=makeQuery(id+"F7.imprint","INTERSECT",VERTEX,{"derivedFrom":[subQ1,subQ0]});Q49=makeQuery(id+"F7.imprint","IMPRINT",FACE,{"disambiguationData":[TD([[makeQuery(id+"F7.imprint","IMPRINT",EDGE,{"disambiguationData":[TD([[subQ2,-1.0]])],"derivedFrom":subQ1}),1.0]])]});}
            var Q50;
            {var subQ0=sQuery(id+"F7.wireOp",EDGE,"E34.top");var subQ1=sQuery(id+"F7.wireOp",EDGE,"E31.right");var subQ2=makeQuery(id+"F7.imprint","INTERSECT",VERTEX,{"derivedFrom":[subQ1,subQ0]});Q50=makeQuery(id+"F7.imprint","IMPRINT",FACE,{"disambiguationData":[TD([[makeQuery(id+"F7.imprint","IMPRINT",EDGE,{"disambiguationData":[TD([[subQ2,-1.0]])],"derivedFrom":subQ1}),1.0]])]});}
            var Q51;
            {var subQ0=sQuery(id+"F7.wireOp",EDGE,"E40.top");var subQ1=sQuery(id+"F7.wireOp",EDGE,"E32.left");var subQ2=makeQuery(id+"F7.imprint","INTERSECT",VERTEX,{"derivedFrom":[subQ1,subQ0]});Q51=makeQuery(id+"F7.imprint","IMPRINT",FACE,{"disambiguationData":[TD([[makeQuery(id+"F7.imprint","IMPRINT",EDGE,{"disambiguationData":[TD([[subQ2,-1.0]])],"derivedFrom":subQ1}),1.0]])]});}
            var Q52;
            {var subQ0=sQuery(id+"F7.wireOp",EDGE,"E34.top");var subQ1=sQuery(id+"F7.wireOp",EDGE,"E32.left");var subQ2=makeQuery(id+"F7.imprint","INTERSECT",VERTEX,{"derivedFrom":[subQ1,subQ0]});Q52=makeQuery(id+"F7.imprint","IMPRINT",FACE,{"disambiguationData":[TD([[makeQuery(id+"F7.imprint","IMPRINT",EDGE,{"disambiguationData":[TD([[subQ2,-1.0]])],"derivedFrom":subQ1}),1.0]])]});}
            var Q53;
            {var subQ0=sQuery(id+"F7.wireOp",EDGE,"E35.top");var subQ1=sQuery(id+"F7.wireOp",EDGE,"E31.left");var subQ2=makeQuery(id+"F7.imprint","INTERSECT",VERTEX,{"derivedFrom":[subQ1,subQ0]});Q53=makeQuery(id+"F7.imprint","IMPRINT",FACE,{"disambiguationData":[TD([[makeQuery(id+"F7.imprint","IMPRINT",EDGE,{"disambiguationData":[TD([[subQ2,-1.0]])],"derivedFrom":subQ1}),-1.0]])]});}
            var Q54;
            {var subQ0=sQuery(id+"F7.wireOp",EDGE,"E35.top");var subQ1=sQuery(id+"F7.wireOp",EDGE,"E31.left");var subQ2=makeQuery(id+"F7.imprint","INTERSECT",VERTEX,{"derivedFrom":[subQ1,subQ0]});Q54=makeQuery(id+"F7.imprint","IMPRINT",FACE,{"disambiguationData":[TD([[makeQuery(id+"F7.imprint","IMPRINT",EDGE,{"disambiguationData":[TD([[subQ2,-1.0]])],"derivedFrom":subQ1}),1.0]])]});}
            var Q55;
            {var subQ0=sQuery(id+"F7.wireOp",EDGE,"E35.top");var subQ1=sQuery(id+"F7.wireOp",EDGE,"E31.right");var subQ2=makeQuery(id+"F7.imprint","INTERSECT",VERTEX,{"derivedFrom":[subQ1,subQ0]});Q55=makeQuery(id+"F7.imprint","IMPRINT",FACE,{"disambiguationData":[TD([[makeQuery(id+"F7.imprint","IMPRINT",EDGE,{"disambiguationData":[TD([[subQ2,-1.0]])],"derivedFrom":subQ1}),1.0]])]});}
            var Q56;
            {var subQ0=sQuery(id+"F7.wireOp",EDGE,"E35.top");var subQ1=sQuery(id+"F7.wireOp",EDGE,"E32.left");var subQ2=makeQuery(id+"F7.imprint","INTERSECT",VERTEX,{"derivedFrom":[subQ1,subQ0]});Q56=makeQuery(id+"F7.imprint","IMPRINT",FACE,{"disambiguationData":[TD([[makeQuery(id+"F7.imprint","IMPRINT",EDGE,{"disambiguationData":[TD([[subQ2,-1.0]])],"derivedFrom":subQ1}),1.0]])]});}
            var Q57;
            {var subQ0=sQuery(id+"F7.wireOp",EDGE,"E35.top");var subQ1=sQuery(id+"F7.wireOp",EDGE,"E32.right");var subQ2=makeQuery(id+"F7.imprint","INTERSECT",VERTEX,{"derivedFrom":[subQ1,subQ0]});Q57=makeQuery(id+"F7.imprint","IMPRINT",FACE,{"disambiguationData":[TD([[makeQuery(id+"F7.imprint","IMPRINT",EDGE,{"disambiguationData":[TD([[subQ2,-1.0]])],"derivedFrom":subQ1}),1.0]])]});}
            var Q58;
            {var subQ0=sQuery(id+"F7.wireOp",EDGE,"E35.top");var subQ1=sQuery(id+"F7.wireOp",EDGE,"E33.left");var subQ2=makeQuery(id+"F7.imprint","INTERSECT",VERTEX,{"derivedFrom":[subQ1,subQ0]});Q58=makeQuery(id+"F7.imprint","IMPRINT",FACE,{"disambiguationData":[TD([[makeQuery(id+"F7.imprint","IMPRINT",EDGE,{"disambiguationData":[TD([[subQ2,-1.0]])],"derivedFrom":subQ1}),1.0]])]});}
            var Q59;
            {var subQ0=sQuery(id+"F7.wireOp",EDGE,"E35.top");var subQ1=sQuery(id+"F7.wireOp",EDGE,"E33.right");var subQ2=makeQuery(id+"F7.imprint","INTERSECT",VERTEX,{"derivedFrom":[subQ1,subQ0]});Q59=makeQuery(id+"F7.imprint","IMPRINT",FACE,{"disambiguationData":[TD([[makeQuery(id+"F7.imprint","IMPRINT",EDGE,{"disambiguationData":[TD([[subQ2,-1.0]])],"derivedFrom":subQ1}),1.0]])]});}
            var Q60;
            {var subQ0=sQuery(id+"F7.wireOp",EDGE,"E34.top");var subQ1=sQuery(id+"F7.wireOp",EDGE,"E32.right");var subQ2=makeQuery(id+"F7.imprint","INTERSECT",VERTEX,{"derivedFrom":[subQ1,subQ0]});Q60=makeQuery(id+"F7.imprint","IMPRINT",FACE,{"disambiguationData":[TD([[makeQuery(id+"F7.imprint","IMPRINT",EDGE,{"disambiguationData":[TD([[subQ2,-1.0]])],"derivedFrom":subQ1}),1.0]])]});}
            var Q61;
            {var subQ0=sQuery(id+"F7.wireOp",EDGE,"E34.bottom");var subQ1=sQuery(id+"F7.wireOp",EDGE,"E33.left");var subQ2=makeQuery(id+"F7.imprint","INTERSECT",VERTEX,{"derivedFrom":[subQ1,subQ0]});Q61=makeQuery(id+"F7.imprint","IMPRINT",FACE,{"disambiguationData":[TD([[makeQuery(id+"F7.imprint","IMPRINT",EDGE,{"disambiguationData":[TD([[subQ2,-1.0]])],"derivedFrom":subQ1}),1.0]])]});}
            var Q62;
            {var subQ0=sQuery(id+"F7.wireOp",EDGE,"E34.bottom");var subQ1=sQuery(id+"F7.wireOp",EDGE,"E32.left");var subQ2=makeQuery(id+"F7.imprint","INTERSECT",VERTEX,{"derivedFrom":[subQ1,subQ0]});Q62=makeQuery(id+"F7.imprint","IMPRINT",FACE,{"disambiguationData":[TD([[makeQuery(id+"F7.imprint","IMPRINT",EDGE,{"disambiguationData":[TD([[subQ2,-1.0]])],"derivedFrom":subQ1}),1.0]])]});}
            var Q63;
            {var subQ0=sQuery(id+"F7.wireOp",EDGE,"E34.bottom");var subQ1=sQuery(id+"F7.wireOp",EDGE,"E31.left");var subQ2=makeQuery(id+"F7.imprint","INTERSECT",VERTEX,{"derivedFrom":[subQ1,subQ0]});Q63=makeQuery(id+"F7.imprint","IMPRINT",FACE,{"disambiguationData":[TD([[makeQuery(id+"F7.imprint","IMPRINT",EDGE,{"disambiguationData":[TD([[subQ2,-1.0]])],"derivedFrom":subQ1}),1.0]])]});}
            var Q64;
            {var subQ0=sQuery(id+"F7.wireOp",EDGE,"E36.top");var subQ1=sQuery(id+"F7.wireOp",EDGE,"E31.left");var subQ2=makeQuery(id+"F7.imprint","INTERSECT",VERTEX,{"derivedFrom":[subQ1,subQ0]});Q64=makeQuery(id+"F7.imprint","IMPRINT",FACE,{"disambiguationData":[TD([[makeQuery(id+"F7.imprint","IMPRINT",EDGE,{"disambiguationData":[TD([[subQ2,-1.0]])],"derivedFrom":subQ1}),-1.0]])]});}
            var Q65;
            {var subQ0=sQuery(id+"F7.wireOp",EDGE,"E36.bottom");var subQ1=sQuery(id+"F7.wireOp",EDGE,"E31.left");var subQ2=makeQuery(id+"F7.imprint","INTERSECT",VERTEX,{"derivedFrom":[subQ1,subQ0]});Q65=makeQuery(id+"F7.imprint","IMPRINT",FACE,{"disambiguationData":[TD([[makeQuery(id+"F7.imprint","IMPRINT",EDGE,{"disambiguationData":[TD([[subQ2,-1.0]])],"derivedFrom":subQ1}),1.0]])]});}
            var Q66;
            {var subQ0=sQuery(id+"F7.wireOp",EDGE,"E36.top");var subQ1=sQuery(id+"F7.wireOp",EDGE,"E31.left");var subQ2=makeQuery(id+"F7.imprint","INTERSECT",VERTEX,{"derivedFrom":[subQ1,subQ0]});Q66=makeQuery(id+"F7.imprint","IMPRINT",FACE,{"disambiguationData":[TD([[makeQuery(id+"F7.imprint","IMPRINT",EDGE,{"disambiguationData":[TD([[subQ2,-1.0]])],"derivedFrom":subQ1}),1.0]])]});}
            var Q67;
            {var subQ0=sQuery(id+"F7.wireOp",EDGE,"E36.bottom");var subQ1=sQuery(id+"F7.wireOp",EDGE,"E32.left");var subQ2=makeQuery(id+"F7.imprint","INTERSECT",VERTEX,{"derivedFrom":[subQ1,subQ0]});Q67=makeQuery(id+"F7.imprint","IMPRINT",FACE,{"disambiguationData":[TD([[makeQuery(id+"F7.imprint","IMPRINT",EDGE,{"disambiguationData":[TD([[subQ2,-1.0]])],"derivedFrom":subQ1}),1.0]])]});}
            var Q68;
            {var subQ0=sQuery(id+"F7.wireOp",EDGE,"E36.top");var subQ1=sQuery(id+"F7.wireOp",EDGE,"E32.left");var subQ2=makeQuery(id+"F7.imprint","INTERSECT",VERTEX,{"derivedFrom":[subQ1,subQ0]});Q68=makeQuery(id+"F7.imprint","IMPRINT",FACE,{"disambiguationData":[TD([[makeQuery(id+"F7.imprint","IMPRINT",EDGE,{"disambiguationData":[TD([[subQ2,-1.0]])],"derivedFrom":subQ1}),1.0]])]});}
            var Q69;
            {var subQ0=sQuery(id+"F7.wireOp",EDGE,"E36.top");var subQ1=sQuery(id+"F7.wireOp",EDGE,"E32.right");var subQ2=makeQuery(id+"F7.imprint","INTERSECT",VERTEX,{"derivedFrom":[subQ1,subQ0]});Q69=makeQuery(id+"F7.imprint","IMPRINT",FACE,{"disambiguationData":[TD([[makeQuery(id+"F7.imprint","IMPRINT",EDGE,{"disambiguationData":[TD([[subQ2,-1.0]])],"derivedFrom":subQ1}),1.0]])]});}
            var Q70;
            {var subQ0=sQuery(id+"F7.wireOp",EDGE,"E36.top");var subQ1=sQuery(id+"F7.wireOp",EDGE,"E31.right");var subQ2=makeQuery(id+"F7.imprint","INTERSECT",VERTEX,{"derivedFrom":[subQ1,subQ0]});Q70=makeQuery(id+"F7.imprint","IMPRINT",FACE,{"disambiguationData":[TD([[makeQuery(id+"F7.imprint","IMPRINT",EDGE,{"disambiguationData":[TD([[subQ2,-1.0]])],"derivedFrom":subQ1}),1.0]])]});}
            var Q71;
            {var subQ0=sQuery(id+"F7.wireOp",EDGE,"E36.bottom");var subQ1=sQuery(id+"F7.wireOp",EDGE,"E33.left");var subQ2=makeQuery(id+"F7.imprint","INTERSECT",VERTEX,{"derivedFrom":[subQ1,subQ0]});Q71=makeQuery(id+"F7.imprint","IMPRINT",FACE,{"disambiguationData":[TD([[makeQuery(id+"F7.imprint","IMPRINT",EDGE,{"disambiguationData":[TD([[subQ2,-1.0]])],"derivedFrom":subQ1}),1.0]])]});}
            var Q72;
            {var subQ0=sQuery(id+"F7.wireOp",EDGE,"E36.top");var subQ1=sQuery(id+"F7.wireOp",EDGE,"E33.left");var subQ2=makeQuery(id+"F7.imprint","INTERSECT",VERTEX,{"derivedFrom":[subQ1,subQ0]});Q72=makeQuery(id+"F7.imprint","IMPRINT",FACE,{"disambiguationData":[TD([[makeQuery(id+"F7.imprint","IMPRINT",EDGE,{"disambiguationData":[TD([[subQ2,-1.0]])],"derivedFrom":subQ1}),1.0]])]});}
            var Q73;
            {var subQ0=sQuery(id+"F7.wireOp",EDGE,"E36.top");var subQ1=sQuery(id+"F7.wireOp",EDGE,"E33.right");var subQ2=makeQuery(id+"F7.imprint","INTERSECT",VERTEX,{"derivedFrom":[subQ1,subQ0]});Q73=makeQuery(id+"F7.imprint","IMPRINT",FACE,{"disambiguationData":[TD([[makeQuery(id+"F7.imprint","IMPRINT",EDGE,{"disambiguationData":[TD([[subQ2,-1.0]])],"derivedFrom":subQ1}),1.0]])]});}
            var Q74;
            {var subQ0=sQuery(id+"F7.wireOp",EDGE,"E35.bottom");var subQ1=sQuery(id+"F7.wireOp",EDGE,"E33.left");var subQ2=makeQuery(id+"F7.imprint","INTERSECT",VERTEX,{"derivedFrom":[subQ1,subQ0]});Q74=makeQuery(id+"F7.imprint","IMPRINT",FACE,{"disambiguationData":[TD([[makeQuery(id+"F7.imprint","IMPRINT",EDGE,{"disambiguationData":[TD([[subQ2,-1.0]])],"derivedFrom":subQ1}),1.0]])]});}
            var Q75;
            {var subQ0=sQuery(id+"F7.wireOp",EDGE,"E35.bottom");var subQ1=sQuery(id+"F7.wireOp",EDGE,"E32.left");var subQ2=makeQuery(id+"F7.imprint","INTERSECT",VERTEX,{"derivedFrom":[subQ1,subQ0]});Q75=makeQuery(id+"F7.imprint","IMPRINT",FACE,{"disambiguationData":[TD([[makeQuery(id+"F7.imprint","IMPRINT",EDGE,{"disambiguationData":[TD([[subQ2,-1.0]])],"derivedFrom":subQ1}),1.0]])]});}
            var Q76;
            {var subQ0=sQuery(id+"F7.wireOp",EDGE,"E35.bottom");var subQ1=sQuery(id+"F7.wireOp",EDGE,"E31.left");var subQ2=makeQuery(id+"F7.imprint","INTERSECT",VERTEX,{"derivedFrom":[subQ1,subQ0]});Q76=makeQuery(id+"F7.imprint","IMPRINT",FACE,{"disambiguationData":[TD([[makeQuery(id+"F7.imprint","IMPRINT",EDGE,{"disambiguationData":[TD([[subQ2,-1.0]])],"derivedFrom":subQ1}),1.0]])]});}
            var Q77;
            Q77=makeQuery(id+"F7.imprint","IMPRINT",FACE,{"disambiguationData":[TD([[makeQuery(id+"F7.imprint","IMPRINT",EDGE,{"derivedFrom":makeQuery(id+"F1.opExtrude","CAP_EDGE",EDGE,{"disambiguationData":[OSD([sQuery(id+"F0.wireOp",EDGE,"E4")])],"isStart":false})}),1.0]])]});
            var Q78;
            Q78=makeQuery(id+"F7.imprint","IMPRINT",FACE,{"disambiguationData":[TD([[makeQuery(id+"F7.imprint","IMPRINT",EDGE,{"derivedFrom":makeQuery(id+"F1.opExtrude","CAP_EDGE",EDGE,{"disambiguationData":[OSD([sQuery(id+"F0.wireOp",EDGE,"E5")])],"isStart":false})}),1.0]])]});
            var Q79;
            Q79=makeQuery(id+"F7.imprint","IMPRINT",FACE,{"disambiguationData":[TD([[makeQuery(id+"F7.imprint","IMPRINT",EDGE,{"derivedFrom":makeQuery(id+"F1.opExtrude","CAP_EDGE",EDGE,{"disambiguationData":[OSD([sQuery(id+"F0.wireOp",EDGE,"E2")])],"isStart":false})}),1.0]])]});
            var Q80;
            {var subQ0=sQuery(id+"F7.wireOp",EDGE,"E31.right");var subQ5=makeQuery(id+"F1.opExtrude","CAP_EDGE",EDGE,{"disambiguationData":[OSD([sQuery(id+"F0.wireOp",EDGE,"E0.top")])],"isStart":false});var subQ6=makeQuery(id+"F7.imprint","INTERSECT",VERTEX,{"derivedFrom":[subQ5,subQ0]});Q80=makeQuery(id+"F7.imprint","IMPRINT",FACE,{"disambiguationData":[TD([[makeQuery(id+"F7.imprint","IMPRINT",EDGE,{"disambiguationData":[TD([[subQ6,-1.0]])],"derivedFrom":subQ5}),-1.0]])]});}
            var Q81;
            {var subQ0=sQuery(id+"F7.wireOp",EDGE,"E32.right");var subQ5=makeQuery(id+"F1.opExtrude","CAP_EDGE",EDGE,{"disambiguationData":[OSD([sQuery(id+"F0.wireOp",EDGE,"E0.top")])],"isStart":false});var subQ6=makeQuery(id+"F7.imprint","INTERSECT",VERTEX,{"derivedFrom":[subQ5,subQ0]});Q81=makeQuery(id+"F7.imprint","IMPRINT",FACE,{"disambiguationData":[TD([[makeQuery(id+"F7.imprint","IMPRINT",EDGE,{"disambiguationData":[TD([[subQ6,-1.0]])],"derivedFrom":subQ5}),-1.0]])]});}
            var Q82;
            {var subQ0=sQuery(id+"F7.wireOp",EDGE,"E40.bottom");var subQ1=sQuery(id+"F7.wireOp",EDGE,"E32.right");var subQ2=makeQuery(id+"F7.imprint","INTERSECT",VERTEX,{"derivedFrom":[subQ1,subQ0]});Q82=makeQuery(id+"F7.imprint","IMPRINT",FACE,{"disambiguationData":[TD([[makeQuery(id+"F7.imprint","IMPRINT",EDGE,{"disambiguationData":[TD([[subQ2,-1.0]])],"derivedFrom":subQ1}),1.0]])]});}
            var Q83;
            {var subQ0=sQuery(id+"F7.wireOp",EDGE,"E40.bottom");var subQ1=sQuery(id+"F7.wireOp",EDGE,"E32.left");var subQ2=makeQuery(id+"F7.imprint","INTERSECT",VERTEX,{"derivedFrom":[subQ1,subQ0]});Q83=makeQuery(id+"F7.imprint","IMPRINT",FACE,{"disambiguationData":[TD([[makeQuery(id+"F7.imprint","IMPRINT",EDGE,{"disambiguationData":[TD([[subQ2,-1.0]])],"derivedFrom":subQ1}),1.0]])]});}
            var Q84;
            {var subQ0=sQuery(id+"F7.wireOp",EDGE,"E40.bottom");var subQ1=sQuery(id+"F7.wireOp",EDGE,"E31.right");var subQ2=makeQuery(id+"F7.imprint","INTERSECT",VERTEX,{"derivedFrom":[subQ1,subQ0]});Q84=makeQuery(id+"F7.imprint","IMPRINT",FACE,{"disambiguationData":[TD([[makeQuery(id+"F7.imprint","IMPRINT",EDGE,{"disambiguationData":[TD([[subQ2,-1.0]])],"derivedFrom":subQ1}),1.0]])]});}
            extrude(context, id + "F8", {"entities" : qUnion([Q0, Q1, Q2, Q3, Q4, Q5, Q6, Q7, Q8, Q9, Q10, Q11, Q12, Q13, Q14, Q15, Q16, Q17, Q18, Q19, Q20, Q21, Q22, Q23, Q24, Q25, Q26, Q27, Q28, Q29, Q30, Q31, Q32, Q33, Q34, Q35, Q36, Q37, Q38, Q39, Q40, Q41, Q42, Q43, Q44, Q45, Q46, Q47, Q48, Q49, Q50, Q51, Q52, Q53, Q54, Q55, Q56, Q57, Q58, Q59, Q60, Q61, Q62, Q63, Q64, Q65, Q66, Q67, Q68, Q69, Q70, Q71, Q72, Q73, Q74, Q75, Q76, Q77, Q78, Q79, Q80, Q81, Q82, Q83, Q84]), "depth" : 2 * mm});
        }
        {
            var Q0;
            Q0=makeQuery(id+"F8.opExtrude","CAP_FACE",FACE,{"disambiguationData":[OSD([sQuery(id+"F7.wireOp",EDGE,"E24.bottom"),sQuery(id+"F7.wireOp",EDGE,"E24.top"),sQuery(id+"F7.wireOp",EDGE,"E24.left"),sQuery(id+"F7.wireOp",EDGE,"E24.right"),sQuery(id+"F7.wireOp",EDGE,"E31.bottom"),sQuery(id+"F7.wireOp",EDGE,"E31.top"),sQuery(id+"F7.wireOp",EDGE,"E31.left"),sQuery(id+"F7.wireOp",EDGE,"E31.right"),sQuery(id+"F7.wireOp",EDGE,"E32.bottom"),sQuery(id+"F7.wireOp",EDGE,"E32.top"),sQuery(id+"F7.wireOp",EDGE,"E32.left"),sQuery(id+"F7.wireOp",EDGE,"E32.right"),sQuery(id+"F7.wireOp",EDGE,"E33.bottom"),sQuery(id+"F7.wireOp",EDGE,"E33.top"),sQuery(id+"F7.wireOp",EDGE,"E33.left"),sQuery(id+"F7.wireOp",EDGE,"E33.right"),sQuery(id+"F7.wireOp",EDGE,"E34.bottom"),sQuery(id+"F7.wireOp",EDGE,"E34.top"),sQuery(id+"F7.wireOp",EDGE,"E34.left"),sQuery(id+"F7.wireOp",EDGE,"E34.right"),sQuery(id+"F7.wireOp",EDGE,"E35.bottom"),sQuery(id+"F7.wireOp",EDGE,"E35.top"),sQuery(id+"F7.wireOp",EDGE,"E35.left"),sQuery(id+"F7.wireOp",EDGE,"E35.right"),sQuery(id+"F7.wireOp",EDGE,"E36.bottom"),sQuery(id+"F7.wireOp",EDGE,"E36.top"),sQuery(id+"F7.wireOp",EDGE,"E36.left"),sQuery(id+"F7.wireOp",EDGE,"E36.right"),sQuery(id+"F7.wireOp",EDGE,"E40.bottom"),sQuery(id+"F7.wireOp",EDGE,"E40.top"),sQuery(id+"F7.wireOp",EDGE,"E40.left"),sQuery(id+"F7.wireOp",EDGE,"E40.right")])],"isStart":false});
            var sketch = newSketch(context, id + "F9", { "sketchPlane" : qUnion([Q0])});
            skCircle(sketch, "E41.0", {"center": v(-34, -34) * mm, "radius": 1.5 * mm});
            skCircle(sketch, "E42.0", {"center": v(-34, 34) * mm, "radius": 1.5 * mm});
            skCircle(sketch, "E43.0", {"center": v(34, 34) * mm, "radius": 1.5 * mm});
            skCircle(sketch, "E44.0", {"center": v(34, -34) * mm, "radius": 1.5 * mm});
            skSolve(sketch);
        }
        {
            var Q0;
            Q0=makeQuery(id+"F9.imprint","IMPRINT",FACE,{"disambiguationData":[TD([[makeQuery(id+"F9.imprint","IMPRINT",EDGE,{"derivedFrom":sQuery(id+"F9.wireOp",EDGE,"E41.0")}),1.0]])]});
            var Q1;
            Q1=makeQuery(id+"F9.imprint","IMPRINT",FACE,{"disambiguationData":[TD([[makeQuery(id+"F9.imprint","IMPRINT",EDGE,{"derivedFrom":sQuery(id+"F9.wireOp",EDGE,"E44.0")}),1.0]])]});
            var Q2;
            Q2=makeQuery(id+"F9.imprint","IMPRINT",FACE,{"disambiguationData":[TD([[makeQuery(id+"F9.imprint","IMPRINT",EDGE,{"derivedFrom":sQuery(id+"F9.wireOp",EDGE,"E43.0")}),1.0]])]});
            var Q3;
            Q3=makeQuery(id+"F9.imprint","IMPRINT",FACE,{"disambiguationData":[TD([[makeQuery(id+"F9.imprint","IMPRINT",EDGE,{"derivedFrom":sQuery(id+"F9.wireOp",EDGE,"E42.0")}),1.0]])]});
            extrude(context, id + "F10", {"entities" : qUnion([Q0, Q1, Q2, Q3]), "operationType" : NewBodyOperationType.REMOVE, "oppositeDirection" : true, "depth" : 2 * mm});
        }
        {
            var Q0;
            Q0 = qSketchRegion(id + "F6", true);
            extrude(context, id + "F11", {"entities" : qUnion([Q0]), "operationType" : NewBodyOperationType.REMOVE, "oppositeDirection" : true, "depth" : 7 * mm});
        }
    });
